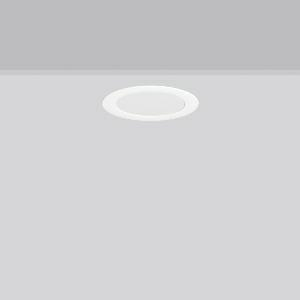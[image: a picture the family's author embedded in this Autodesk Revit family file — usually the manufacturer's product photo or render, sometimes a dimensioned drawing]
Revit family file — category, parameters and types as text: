
# Revit family: toledo_flat_round_e_901452_002_8d3d
name_source: partatom
category: Lighting Fixtures
units: mm (PartAtom-declared; Revit-internal decimal feet)

## family parameters
Cut with Voids When Loaded = No
Host = Face
Light Source = No
Part Type = Normal
Room Calculation Point = No
Round Connector Dimension = Use Diameter
Shared = No

## types (1)
- TOLEDO FLAT round E (1 x LED Modul 830, 780 lm, 3000)
    Apparent Load = 8 VA
    CIE Flux Codes = 47 79 96 100 100
    Color Rendering = 80
    Color Temperature = 3000
    Default Elevation = 1800 mm
    Description = Series: TOLEDO FLAT round
Ultra thin recessed downlight. Housing: die-cast aluminium. Light guide and diffuser made of non-yellowing PMMA, opal matt. Ceiling installation with spring system. Mounting depth depends on ceiling strength. Including separate LED converter with connecting cable 250 mm. Suitable for through-wiring with separately available accessories. Surface mounted housing as accessory for all sizes. Retrofittable decorative cylinders made of chintz fabric as accessory, optional with satin finish plastic diffuser. Through-wiring box (5 pole) available as accessory. 
Colour: white
Diameter: 190 mm
Height: 2.5 mm
Cut-out diameter: 170 mm
Recess height: 27-53 mm
Luminaire: recess height: 31-51 mm
Lamp: LED
Socket: without socket
Colour temperature: 3000K
Colour rendering index (CRI): 80
System power: 7.7 W
Rated luminous flux: 780 lm
Luminous efficiency: 101 lm/W
Control gear: Regulated power supply
Protection class: II
Type of protection: IP 54
    Height = 0 mm  [stored 0 ft]
    Lamp = 1 x LED Modul 830
    Lamp Light Flux = 780 lm
    Lamp count = 1
    Length = 190 mm  [stored 0.62336 ft]
    Lifetime = 50000 h
    Luminous efficacy = 101 lm/W
    Manufacturer = RZB
    ModVariant = No
    Model = 901452.002
    Mounting Place = Ceiling
    Mounting Type = Recessed
    Number of Poles = 1
    OnlyDefault = Yes
    Power Factor = 1
    Product Name = TOLEDO FLAT round E
    Product group = Recessed downlights
    ProductGroupID = 402
    Protection Class = Protection class II
    Protection Degree = IP 20
    RLX_Detail_Level = 1
    RLX_Emergency_Light_Flux = 0 lm
    RLX_Emergency_Type = 0
    RLX_Emergency_Type_DB = No
    RlxData = <blob elided: 75385 chars, md5=97778a2f>
    Socket = socket
    Standby Power = 0 W
    System Light Flux = 780 lm
    System Power = 8 W
    Type Comments = Product without accessories
    Type Image = 901452.002.jpg
    URL = http://relux.com
    VarID = ---
    Voltage = 230 V
    Voltage Range = 220-240 V
    Weight = 0.00 kg
    Width = 0 mm  [stored 0 ft]

note: [stored X ft] marks values corroborated as IEEE doubles in the binary element streams (Revit-internal decimal feet)

## geometry (parser evidence)
native form markers: Blend x4, Sweep x10
no freeform markers — native parametric forms only
